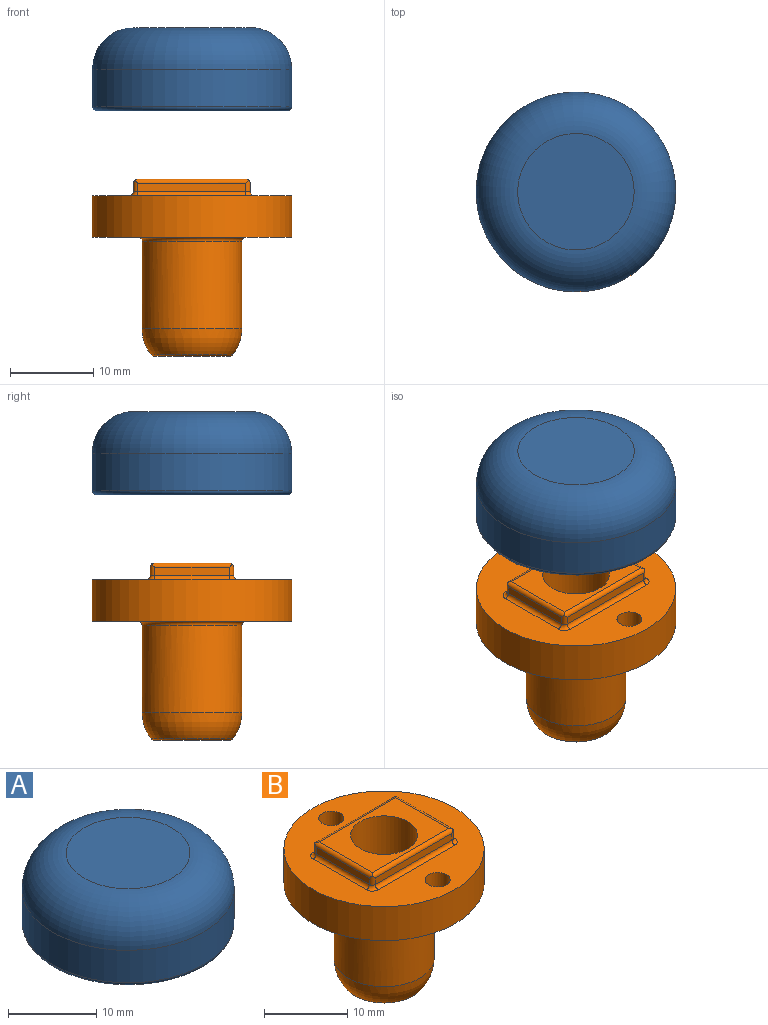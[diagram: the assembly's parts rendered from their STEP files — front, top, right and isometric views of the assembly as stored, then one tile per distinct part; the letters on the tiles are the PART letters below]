
ASSEMBLY  parts=2 mates=1
PART A: 30 faces, bbox 26x26x10 mm
  f0: plane 23x23mm, normal (0,0,-1), area 224.3mm2, adj f16,f17,f20,f21,f24,f25,f26,f27
  f1: cylinder r=12mm len=24mm, axis (0,0,-1), area 339.3mm2, adj f28,f29
  f2: plane 14x14mm, normal (0,0,1), area 153.9mm2, adj f29
  f3: plane 10x7mm, normal (-1,0,0), area 70mm2, adj f13,f22,f23,f27
  f4: plane 14x7mm, normal (0,-1,0), area 98mm2, adj f11,f12,f21,f22
  f5: plane 10x7mm, normal (1,0,0), area 70mm2, adj f8,f11,f15,f16
  f6: plane 14x7mm, normal (0,1,0), area 98mm2, adj f14,f15,f23,f24
  f7: plane 14x10mm, normal (0,0,-1), area 140mm2, adj f8,f12,f13,f14
  f8: cylinder r=0.5mm len=10mm, axis (0,-1,0), area 7.9mm2, adj f5,f7,f9,f10
  f9: sphere r=0.5mm, area 0.4mm2, adj f8,f11,f12
  f10: sphere r=0.5mm, area 0.4mm2, adj f8,f14,f15
  f11: cylinder r=0.5mm len=7mm, axis (0,0,1), area 5.5mm2, adj f4,f5,f9,f17
  f12: cylinder r=0.5mm len=14mm, axis (-1,0,0), area 11mm2, adj f4,f7,f9,f18
  f13: cylinder r=0.5mm len=10mm, axis (0,1,0), area 7.9mm2, adj f3,f7,f18,f19
  f14: cylinder r=0.5mm len=14mm, axis (1,0,0), area 11mm2, adj f6,f7,f10,f19
  f15: cylinder r=0.5mm len=7mm, axis (0,0,-1), area 5.5mm2, adj f5,f6,f10,f20
  f16: cylinder r=0.5mm len=10mm, axis (0,1,0), area 7.9mm2, adj f0,f5,f17,f20
  f17: torus R=1mm, axis (0,0,1), area 0.8mm2, adj f0,f11,f16,f21
  f18: sphere r=0.5mm, area 0.4mm2, adj f12,f13,f22
  f19: sphere r=0.5mm, area 0.4mm2, adj f13,f14,f23
  f20: torus R=1mm, axis (0,0,1), area 0.8mm2, adj f0,f15,f16,f24
  f21: cylinder r=0.5mm len=14mm, axis (1,0,0), area 11mm2, adj f0,f4,f17,f25
  f22: cylinder r=0.5mm len=7mm, axis (0,0,-1), area 5.5mm2, adj f3,f4,f18,f25
  f23: cylinder r=0.5mm len=7mm, axis (0,0,1), area 5.5mm2, adj f3,f6,f19,f26
  f24: cylinder r=0.5mm len=14mm, axis (-1,0,0), area 11mm2, adj f0,f6,f20,f26
  f25: torus R=1mm, axis (0,0,1), area 0.8mm2, adj f0,f21,f22,f27
  f26: torus R=1mm, axis (0,0,1), area 0.8mm2, adj f0,f23,f24,f27
  f27: cylinder r=0.5mm len=10mm, axis (0,-1,0), area 7.9mm2, adj f0,f3,f25,f26
  f28: torus R=11.5mm, axis (0,0,1), area 58.3mm2, adj f0,f1
  f29: torus R=7mm, axis (0,0,1), area 502.5mm2, adj f1,f2
PART B: 33 faces, bbox 24x24x21.3 mm
  f0: cylinder r=12mm len=24mm, axis (0,0,-1), area 377mm2, adj f1,f2
  f1: plane 24x24mm, normal (0,0,1), area 274.1mm2, adj f0,f13,f14,f16,f17,f18,f20,f22
  f2: plane 24x24mm, normal (0,0,-1), area 294.5mm2, adj f0,f25,f31,f32
  f3: plane 9x1mm, normal (1,0,0), area 9mm2, adj f8,f12,f15,f16
  f4: plane 13x1mm, normal (0,1,0), area 13mm2, adj f10,f12,f13,f21
  f5: plane 9x1mm, normal (-1,0,0), area 9mm2, adj f11,f19,f21,f22
  f6: plane 13x1mm, normal (0,-1,0), area 13mm2, adj f9,f15,f18,f19
  f7: plane 13x9mm, normal (0,0,1), area 66.7mm2, adj f8,f9,f10,f11,f26
  f8: cylinder r=0.5mm len=9.71mm, axis (0,-1,0), area 7.4mm2, adj f3,f7,f9,f10,f12,f15
  f9: cylinder r=0.5mm len=13.71mm, axis (-1,0,0), area 10.5mm2, adj f6,f7,f8,f11,f15,f19
  f10: cylinder r=0.5mm len=13.71mm, axis (1,0,0), area 10.5mm2, adj f4,f7,f8,f11,f12,f21
  f11: cylinder r=0.5mm len=9.71mm, axis (0,1,0), area 7.4mm2, adj f5,f7,f9,f10,f19,f21
  f12: cylinder r=0.5mm len=1.35mm, axis (0,0,-1), area 0.9mm2, adj f3,f4,f8,f10,f14
  f13: cylinder r=0.5mm len=13mm, axis (-1,0,0), area 10.2mm2, adj f1,f4,f14,f23
  f14: torus R=1mm, axis (0,0,1), area 0.8mm2, adj f1,f12,f13,f16
  f15: cylinder r=0.5mm len=1.35mm, axis (0,0,1), area 0.9mm2, adj f3,f6,f8,f9,f17
  f16: cylinder r=0.5mm len=9mm, axis (0,1,0), area 7.1mm2, adj f1,f3,f14,f17
  f17: torus R=1mm, axis (0,0,1), area 0.8mm2, adj f1,f15,f16,f18
  f18: cylinder r=0.5mm len=13mm, axis (1,0,0), area 10.2mm2, adj f1,f6,f17,f20
  f19: cylinder r=0.5mm len=1.35mm, axis (0,0,-1), area 0.9mm2, adj f5,f6,f9,f11,f20
  f20: torus R=1mm, axis (0,0,1), area 0.8mm2, adj f1,f18,f19,f22
  f21: cylinder r=0.5mm len=1.35mm, axis (0,0,1), area 0.9mm2, adj f4,f5,f10,f11,f23
  f22: cylinder r=0.5mm len=9mm, axis (0,-1,0), area 7.1mm2, adj f1,f5,f20,f23
  f23: torus R=1mm, axis (0,0,1), area 0.8mm2, adj f1,f13,f21,f22
  f24: cylinder r=6mm len=12mm, axis (0,0,1), area 395.8mm2, adj f25,f27
  f25: torus R=6.5mm, axis (0,0,1), area 30.5mm2, adj f2,f24
  f26: cylinder r=4mm len=20.83mm, axis (0,0,-1), area 523.5mm2, adj f7,f28
  f27: torus R=1mm, axis (0,0,-1), area 120.1mm2, adj f24,f28
  f28: torus R=4.5mm, axis (0,0,1), area 33.8mm2, adj f26,f27
  f29: cylinder r=1.5mm len=4.5mm, axis (0,0,1), area 42.4mm2, adj f1,f31
  f30: cylinder r=1.5mm len=4.5mm, axis (0,0,1), area 42.4mm2, adj f1,f32
  f31: cone r=2mm half-angle=45deg, axis (0,0,-1), area 7.8mm2, adj f2,f29
  f32: cone r=2mm half-angle=45deg, axis (0,0,-1), area 7.8mm2, adj f2,f30
PLACE A t=(-25.45,-21.96,-10.61)mm
PLACE B t=(-25.45,-21.96,-25.81)mm fixed
MATE slider A.f1 <-> B.f0  axis (0,0,1) through (-25.45,-21.96,-0.61)mm
